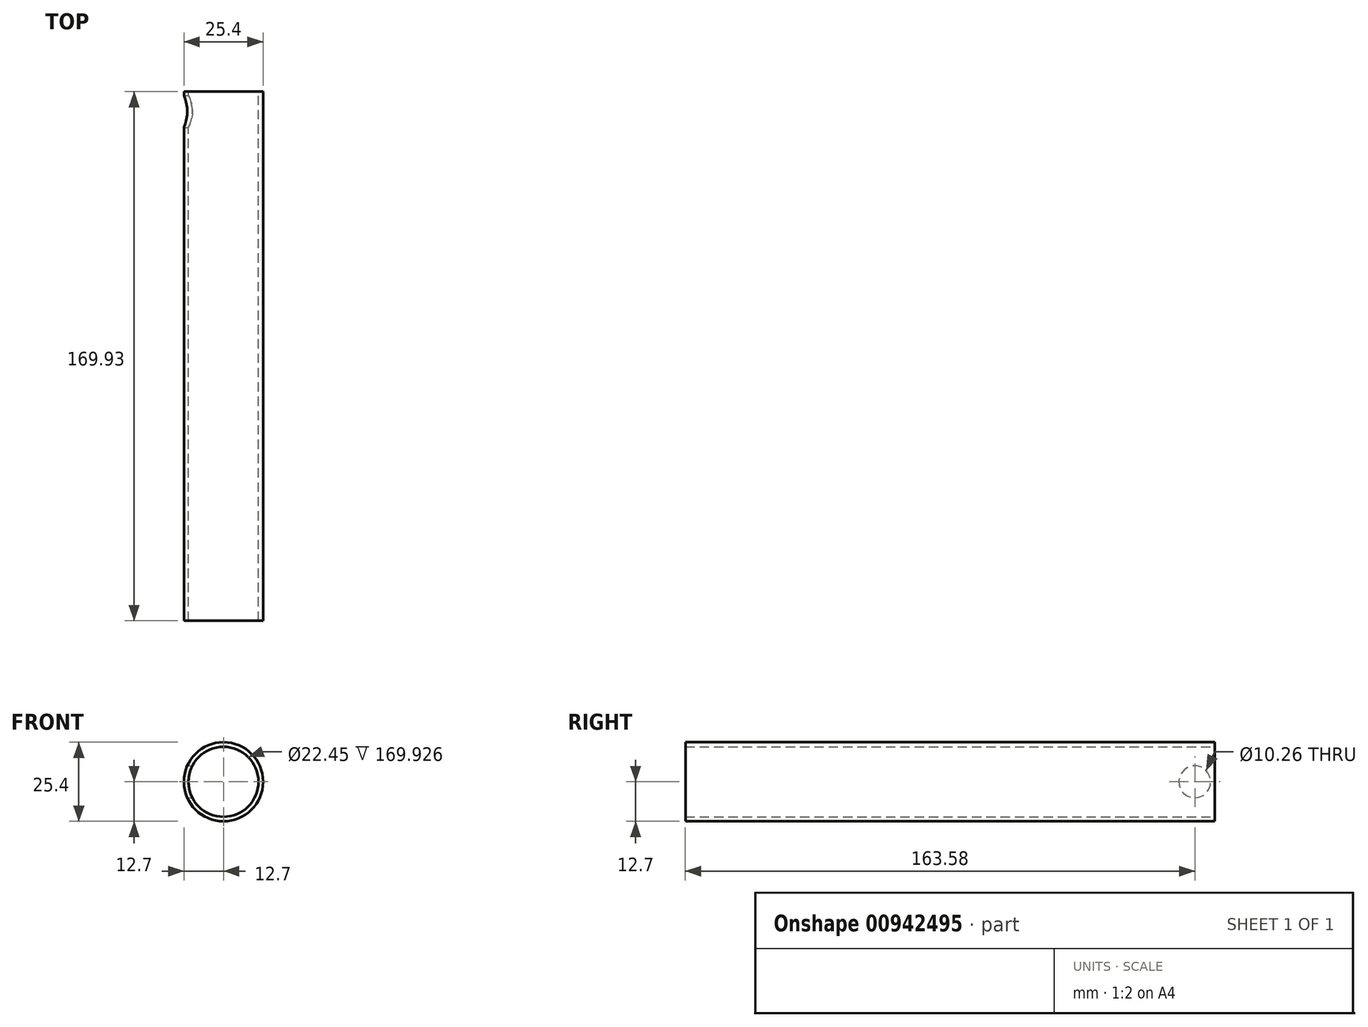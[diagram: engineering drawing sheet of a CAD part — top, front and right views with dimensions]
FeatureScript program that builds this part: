
annotation { "Feature Type Name" : "Feature", "Feature Type Description" : "" }
export const myFeature = defineFeature(function(context is Context, id is Id, definition is map)
    precondition{}
    {
        {
            var Q0;
            Q0=qCreatedBy(makeId("Front.planeOp"),FACE);
            var sketch = newSketch(context, id + "F0", { "sketchPlane" : qUnion([Q0])});
            skCircle(sketch, "E0", {"center": v(0, 0) * mm, "radius": 12.7 * mm});
            skCircle(sketch, "E1", {"center": v(0, 0) * mm, "radius": 11.23 * mm});
            skSolve(sketch);
        }
        {
            var Q0;
            Q0=makeQuery(id+"F0.imprint","IMPRINT",FACE,{"disambiguationData":[TD([[makeQuery(id+"F0.imprint","IMPRINT",EDGE,{"derivedFrom":sQuery(id+"F0.wireOp",EDGE,"E0")}),1.0]])]});
            extrude(context, id + "F1", {"entities" : qUnion([Q0]), "depth" : 169.93 * mm, "offsetDistance" : 25.4 * mm});
        }
        {
            var Q0;
            Q0=qCreatedBy(makeId("Right.planeOp"),FACE);
            var sketch = newSketch(context, id + "F2", { "sketchPlane" : qUnion([Q0])});
            skCircle(sketch, "E2", {"center": v(-6.35, 0) * mm, "radius": 5.13 * mm});
            skSolve(sketch);
        }
        {
            var Q0;
            Q0 = qSketchRegion(id + "F2", true);
            extrude(context, id + "F3", {"entities" : qUnion([Q0]), "operationType" : NewBodyOperationType.REMOVE, "endBound" : BoundingType.THROUGH_ALL, "oppositeDirection" : true, "depth" : 25.4 * mm, "offsetDistance" : 25.4 * mm});
        }
    });
